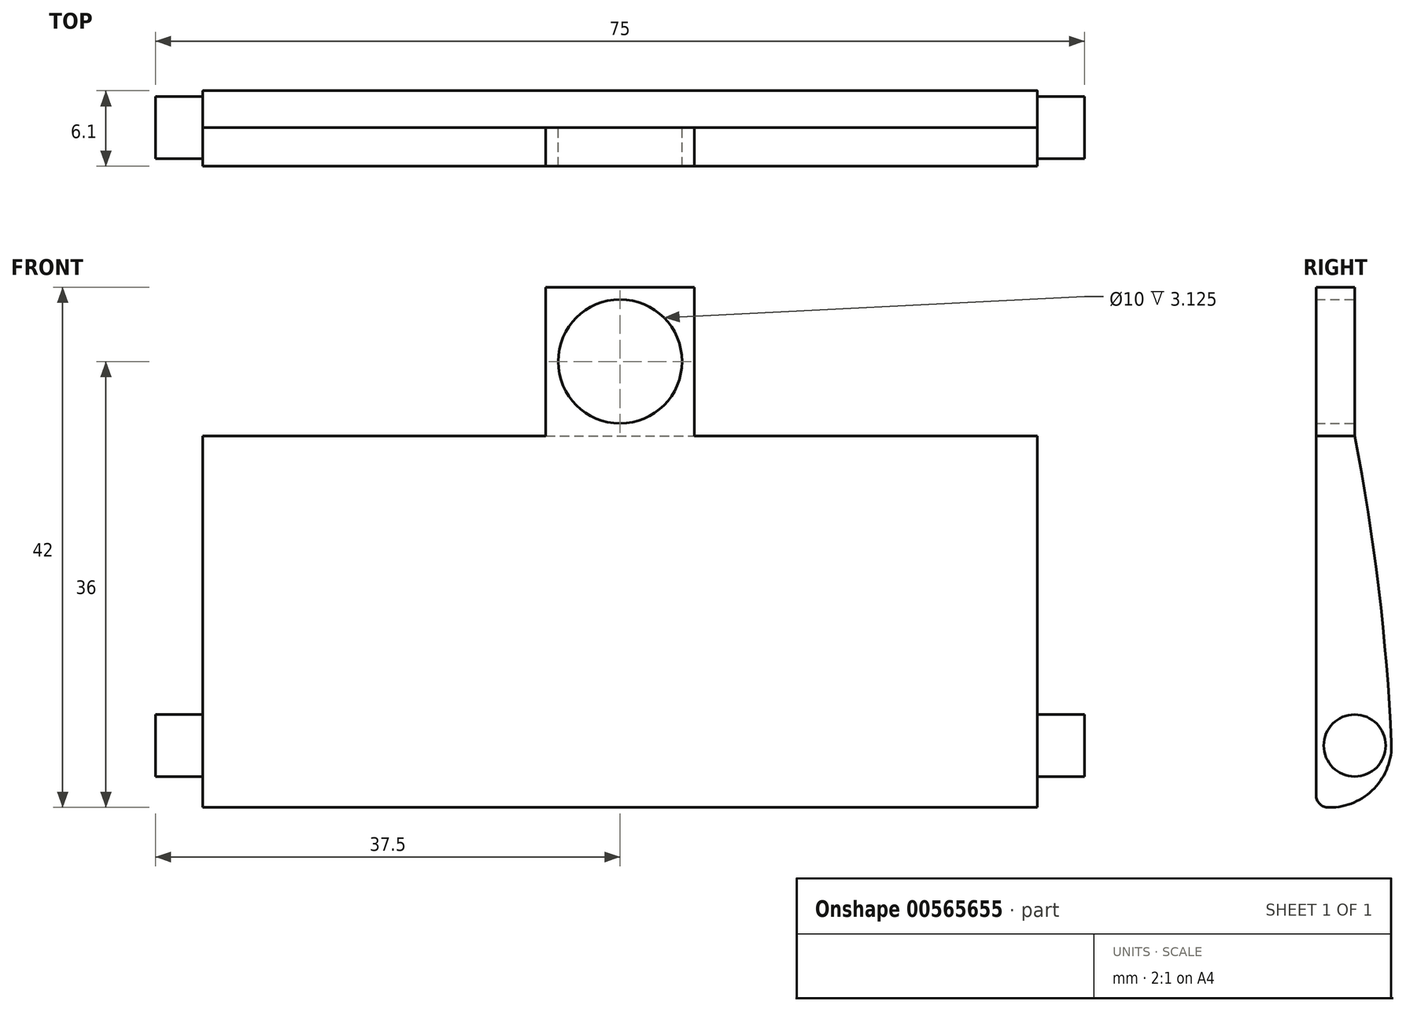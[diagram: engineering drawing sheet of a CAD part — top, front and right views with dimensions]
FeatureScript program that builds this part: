
annotation { "Feature Type Name" : "Feature", "Feature Type Description" : "" }
export const myFeature = defineFeature(function(context is Context, id is Id, definition is map)
    precondition{}
    {
        {
            assignVariable(context, id + "F0", {"name" : "ht", "anyValue" : 25 / 4});
        }
        {
            var Q0;
            Q0=qCreatedBy(makeId("Front.planeOp"),FACE);
            var sketch = newSketch(context, id + "F1", { "sketchPlane" : qUnion([Q0])});
            skLineSegment(sketch, "E0.bottom", {"start": v(-33.7, 15) * mm, "end": v(33.69, 15) * mm});
            skLineSegment(sketch, "E0.top", {"start": v(-33.7, -15) * mm, "end": v(33.69, -15) * mm});
            skLineSegment(sketch, "E0.left", {"start": v(-33.7, 15) * mm, "end": v(-33.7, -15) * mm});
            skLineSegment(sketch, "E0.right", {"start": v(33.69, 15) * mm, "end": v(33.69, -15) * mm});
            skPoint(sketch, "E0.middle", {"position": v(0, 0) * mm});
            skLineSegment(sketch, "E1.bottom", {"start": v(-6, 27) * mm, "end": v(6, 27) * mm});
            skLineSegment(sketch, "E1.left", {"start": v(-6, 27) * mm, "end": v(-6, 15) * mm});
            skLineSegment(sketch, "E1.right", {"start": v(6, 27) * mm, "end": v(6, 15) * mm});
            skPoint(sketch, "E1.middle", {"position": v(0, 15) * mm});
            skLineSegment(sketch, "E2", {"start": v(0, 27) * mm, "end": v(0, 15) * mm, "construction": true});
            skCircle(sketch, "E3", {"center": v(0, 21) * mm, "radius": 5 * mm});
            skLineSegment(sketch, "E4", {"start": v(6, 15) * mm, "end": v(-6, 15) * mm, "construction": true});
            skLineSegment(sketch, "E5", {"start": v(-6, 21) * mm, "end": v(-5, 21) * mm, "construction": true});
            skLineSegment(sketch, "E6", {"start": v(6, 21) * mm, "end": v(5, 21) * mm, "construction": true});
            skSolve(sketch);
        }
        {
            var Q0;
            Q0=makeQuery(id+"F1.imprint","IMPRINT",FACE,{"disambiguationData":[TD([[makeQuery(id+"F1.imprint","IMPRINT",EDGE,{"derivedFrom":sQuery(id+"F1.wireOp",EDGE,"E0.top")}),1.0]])]});
            extrude(context, id + "F2", {"entities" : qUnion([Q0]), "endBound" : BoundingType.SYMMETRIC, "depth" : (getVariable(context, 'ht')) * mm, "offsetDistance" : 25 * mm});
        }
        {
            var Q0;
            Q0=makeQuery(id+"F1.imprint","IMPRINT",FACE,{"disambiguationData":[TD([[makeQuery(id+"F1.imprint","IMPRINT",EDGE,{"derivedFrom":sQuery(id+"F1.wireOp",EDGE,"E1.bottom")}),-1.0]])]});
            var Q1;
            Q1=makeQuery(id+"F2.opExtrude","CAP_FACE",FACE,{"disambiguationData":[OSD([sQuery(id+"F1.wireOp",EDGE,"E0.bottom"),sQuery(id+"F1.wireOp",EDGE,"E0.top"),sQuery(id+"F1.wireOp",EDGE,"E0.left"),sQuery(id+"F1.wireOp",EDGE,"E0.right")])],"isStart":false});
            var Q2;
            Q2=makeQuery(id+"F2.opExtrude","SWEPT_BODY",BODY,{"disambiguationData":[OSD([sQuery(id+"F1.wireOp",EDGE,"E0.bottom"),sQuery(id+"F1.wireOp",EDGE,"E0.top"),sQuery(id+"F1.wireOp",EDGE,"E0.left"),sQuery(id+"F1.wireOp",EDGE,"E0.right")])]});
            extrude(context, id + "F3", {"entities" : qUnion([Q0]), "operationType" : NewBodyOperationType.ADD, "endBound" : BoundingType.UP_TO_SURFACE, "depth" : (25 / 4) * mm, "endBoundEntityFace" : qUnion([Q1]), "endBoundEntityBody" : qUnion([Q2]), "offsetDistance" : 25 * mm});
        }
        {
            var Q0;
            Q0=makeQuery(id+"F2.opExtrude","SWEPT_FACE",FACE,{"disambiguationData":[OSD([sQuery(id+"F1.wireOp",EDGE,"E0.right")])]});
            var sketch = newSketch(context, id + "F4", { "sketchPlane" : qUnion([Q0])});
            skLineSegment(sketch, "E7", {"start": v(-3.12, -15) * mm, "end": v(3.12, -15) * mm, "construction": true});
            skLineSegment(sketch, "E8.0", {"start": v(-3.12, -10) * mm, "end": v(3.12, -10) * mm, "construction": true});
            skCircle(sketch, "E9", {"center": v(0, -10) * mm, "radius": 2.5 * mm});
            skArc(sketch, "E10", {"start": v(3.12, -15) * mm, "mid": v(2.23, 0.07) * mm, "end": v(0, 15) * mm});
            skSolve(sketch);
        }
        {
            var Q0;
            Q0=makeQuery(id+"F2.opExtrude","SWEPT_FACE",FACE,{"disambiguationData":[OSD([sQuery(id+"F1.wireOp",EDGE,"E0.left")])]});
            var sketch = newSketch(context, id + "F5", { "sketchPlane" : qUnion([Q0])});
            skLineSegment(sketch, "E11", {"start": v(-3.13, -15) * mm, "end": v(3.13, -15) * mm, "construction": true});
            skLineSegment(sketch, "E12.0", {"start": v(-3.13, -10) * mm, "end": v(3.13, -10) * mm, "construction": true});
            skCircle(sketch, "E13", {"center": v(0, -10) * mm, "radius": 2.5 * mm});
            skArc(sketch, "E14", {"start": v(0, 15) * mm, "mid": v(-2.34, 0.08) * mm, "end": v(-3.13, -15) * mm});
            skSolve(sketch);
        }
        {
            var Q0;
            Q0=makeQuery(id+"F4.imprint","IMPRINT",FACE,{"disambiguationData":[TD([[makeQuery(id+"F4.imprint","IMPRINT",EDGE,{"derivedFrom":sQuery(id+"F4.wireOp",EDGE,"E9")}),1.0]])]});
            extrude(context, id + "F6", {"entities" : qUnion([Q0]), "operationType" : NewBodyOperationType.ADD, "depth" : 3.8 * mm, "offsetDistance" : 25 * mm});
        }
        {
            var Q0;
            Q0=makeQuery(id+"F5.imprint","IMPRINT",FACE,{"disambiguationData":[TD([[makeQuery(id+"F5.imprint","IMPRINT",EDGE,{"derivedFrom":sQuery(id+"F5.wireOp",EDGE,"E13")}),1.0]])]});
            extrude(context, id + "F7", {"entities" : qUnion([Q0]), "operationType" : NewBodyOperationType.ADD, "depth" : 3.8 * mm, "offsetDistance" : 25 * mm});
        }
        {
            var Q0;
            {var subQ0=sQuery(id+"F4.wireOp",EDGE,"E10");Q0=makeQuery(id+"F4.imprint","IMPRINT",FACE,{"disambiguationData":[TD([[makeQuery(id+"F4.imprint","IMPRINT",EDGE,{"derivedFrom":subQ0}),-1.0]])]});}
            var Q1;
            Q1=makeQuery(id+"F2.opExtrude","SWEPT_FACE",FACE,{"disambiguationData":[OSD([sQuery(id+"F1.wireOp",EDGE,"E0.left")])]});
            extrude(context, id + "F8", {"entities" : qUnion([Q0]), "operationType" : NewBodyOperationType.REMOVE, "endBound" : BoundingType.UP_TO_SURFACE, "oppositeDirection" : true, "depth" : 25 * mm, "endBoundEntityFace" : qUnion([Q1]), "offsetDistance" : 25 * mm});
        }
        {
            var Q0;
            {var subQ0=sQuery(id+"F1.wireOp",EDGE,"E0.top");Q0=makeQuery(id+"F8.boolean.opBoolean","MERGE",EDGE,{"derivedFrom":[makeQuery(id+"F2.opExtrude","CAP_EDGE",EDGE,{"disambiguationData":[OSD([subQ0])],"isStart":true}),makeQuery(id+"F8.opExtrude","SWEPT_EDGE",EDGE,{"disambiguationData":[OSD([subQ0,sQuery(id+"F1.wireOp",EDGE,"E0.right"),sQuery(id+"F4.wireOp",EDGE,"E10")])]})]});}
            fillet(context, id + "F9", {"entities" : qUnion([Q0]), "radius" : 5 * mm, "tangentPropagation" : true, "allowEdgeOverflow" : false});
        }
        {
            var Q0;
            Q0=makeQuery(id+"F2.opExtrude","CAP_EDGE",EDGE,{"disambiguationData":[OSD([sQuery(id+"F1.wireOp",EDGE,"E0.top")])],"isStart":false});
            fillet(context, id + "F10", {"entities" : qUnion([Q0]), "radius" : 1 * mm, "tangentPropagation" : true, "allowEdgeOverflow" : false});
        }
    });
